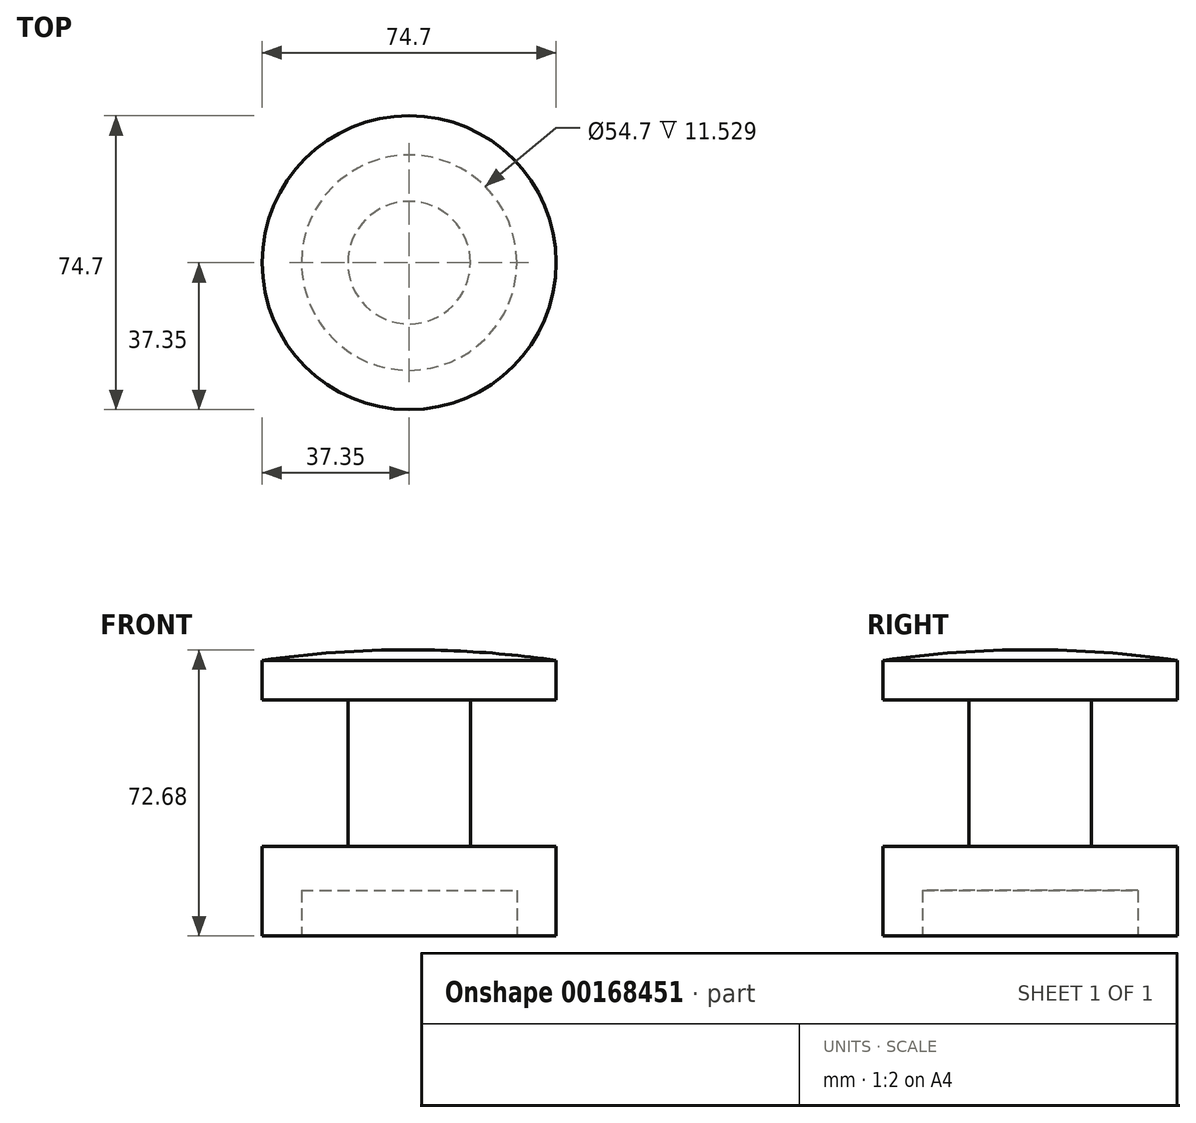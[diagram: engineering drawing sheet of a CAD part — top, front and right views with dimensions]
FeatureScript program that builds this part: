
annotation { "Feature Type Name" : "Feature", "Feature Type Description" : "" }
export const myFeature = defineFeature(function(context is Context, id is Id, definition is map)
    precondition{}
    {
        {
            var Q0;
            Q0=qCreatedBy(makeId("Front.planeOp"),FACE);
            var sketch = newSketch(context, id + "F0", { "sketchPlane" : qUnion([Q0])});
            skLineSegment(sketch, "E0", {"start": v(0, 37.3) * mm, "end": v(0, 50) * mm});
            skLineSegment(sketch, "E1", {"start": v(27.35, 0) * mm, "end": v(37.35, 0) * mm});
            skLineSegment(sketch, "E2", {"start": v(0, 50) * mm, "end": v(0, 37.3) * mm, "construction": true});
            skArc(sketch, "E3", {"start": v(0, 50) * mm, "mid": v(18.72, 49.32) * mm, "end": v(37.35, 47.3) * mm});
            skPoint(sketch, "E4", {"position": v(0, 0) * mm});
            skLineSegment(sketch, "E5.trimOffspring", {"start": v(0, 0) * mm, "end": v(0, -210) * mm, "construction": true});
            skLineSegment(sketch, "E6", {"start": v(15.57, 37.3) * mm, "end": v(15.57, 0) * mm});
            skLineSegment(sketch, "E7", {"start": v(37.35, 0) * mm, "end": v(15.57, 0) * mm});
            skLineSegment(sketch, "E8", {"start": v(0, 0) * mm, "end": v(0, 37.3) * mm});
            skLineSegment(sketch, "E9", {"start": v(37.35, 37.3) * mm, "end": v(37.35, 47.3) * mm});
            skLineSegment(sketch, "E10", {"start": v(15.57, 37.3) * mm, "end": v(37.35, 37.3) * mm});
            skLineSegment(sketch, "E11", {"start": v(37.35, 0) * mm, "end": v(37.35, -22.68) * mm});
            skLineSegment(sketch, "E12", {"start": v(37.35, -22.68) * mm, "end": v(27.35, -22.68) * mm});
            skLineSegment(sketch, "E13", {"start": v(27.35, -22.68) * mm, "end": v(27.35, -11.15) * mm});
            skLineSegment(sketch, "E14", {"start": v(27.35, -11.15) * mm, "end": v(0, -11.15) * mm});
            skLineSegment(sketch, "E15", {"start": v(0, -11.15) * mm, "end": v(0, 0) * mm});
            skSolve(sketch);
        }
        {
            var Q0;
            Q0=makeQuery(id+"F0.imprint","IMPRINT",FACE,{"disambiguationData":[TD([[makeQuery(id+"F0.imprint","IMPRINT",EDGE,{"derivedFrom":sQuery(id+"F0.wireOp",EDGE,"E0")}),-1.0]])]});
            var Q1;
            Q1=sQuery(id+"F0.wireOp",EDGE,"E0");
            revolve(context, id + "F1", {"entities" : qUnion([Q0]), "axis" : qUnion([Q1]), "revolveType" : RevolveType.FULL});
        }
    });
